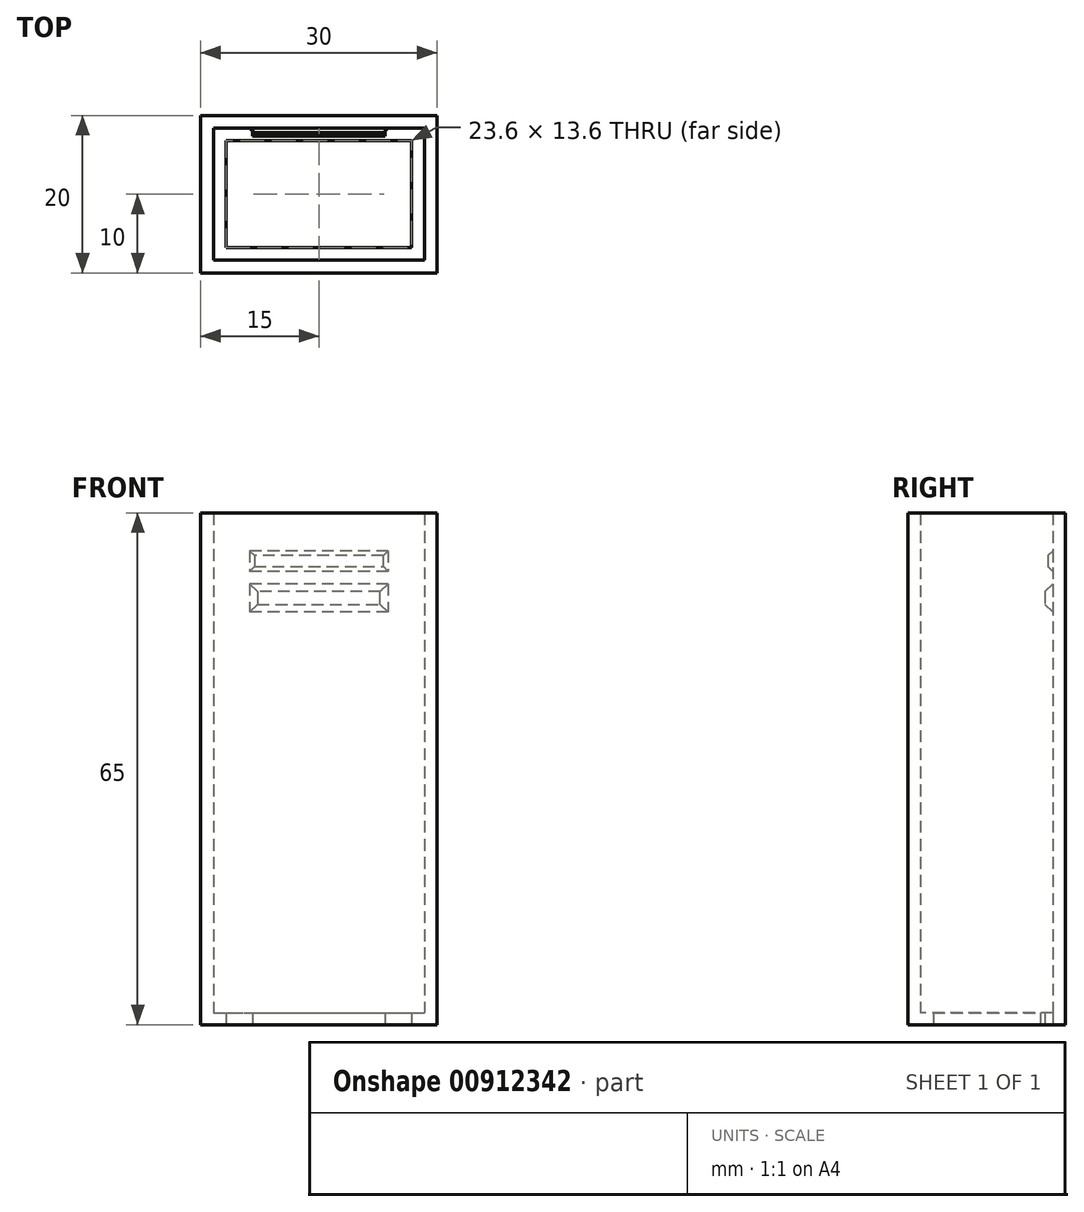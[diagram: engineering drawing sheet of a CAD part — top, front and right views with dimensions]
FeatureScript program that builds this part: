
annotation { "Feature Type Name" : "Feature", "Feature Type Description" : "" }
export const myFeature = defineFeature(function(context is Context, id is Id, definition is map)
    precondition{}
    {
        {
            var Q0;
            Q0=qCreatedBy(makeId("Top.planeOp"),FACE);
            var sketch = newSketch(context, id + "F0", { "sketchPlane" : qUnion([Q0])});
            skPoint(sketch, "E0.middle", {"position": v(0, 0) * mm});
            skLineSegment(sketch, "E1.bottom", {"start": v(-90, 80) * mm, "end": v(-60, 80) * mm});
            skLineSegment(sketch, "E1.top", {"start": v(-90, 60) * mm, "end": v(-60, 60) * mm});
            skLineSegment(sketch, "E1.left", {"start": v(-90, 80) * mm, "end": v(-90, 60) * mm});
            skLineSegment(sketch, "E1.right", {"start": v(-60, 80) * mm, "end": v(-60, 60) * mm});
            skLineSegment(sketch, "E2.bottom", {"start": v(-88.4, 78.4) * mm, "end": v(-61.6, 78.4) * mm});
            skLineSegment(sketch, "E2.top", {"start": v(-88.4, 61.6) * mm, "end": v(-61.6, 61.6) * mm});
            skLineSegment(sketch, "E2.left", {"start": v(-88.4, 78.4) * mm, "end": v(-88.4, 61.6) * mm});
            skLineSegment(sketch, "E2.right", {"start": v(-61.6, 78.4) * mm, "end": v(-61.6, 61.6) * mm});
            skLineSegment(sketch, "E3.bottom", {"start": v(-83.4, 78.4) * mm, "end": v(-66.6, 78.4) * mm});
            skLineSegment(sketch, "E3.top", {"start": v(-83.4, 77.4) * mm, "end": v(-66.6, 77.4) * mm});
            skLineSegment(sketch, "E3.left", {"start": v(-83.4, 78.4) * mm, "end": v(-83.4, 77.4) * mm});
            skLineSegment(sketch, "E3.right", {"start": v(-66.6, 78.4) * mm, "end": v(-66.6, 77.4) * mm});
            skLineSegment(sketch, "E4.bottom", {"start": v(-86.8, 63.2) * mm, "end": v(-63.2, 63.2) * mm});
            skLineSegment(sketch, "E4.top", {"start": v(-86.8, 76.8) * mm, "end": v(-63.2, 76.8) * mm});
            skLineSegment(sketch, "E4.left", {"start": v(-86.8, 63.2) * mm, "end": v(-86.8, 76.8) * mm});
            skLineSegment(sketch, "E4.right", {"start": v(-63.2, 63.2) * mm, "end": v(-63.2, 76.8) * mm});
            skSolve(sketch);
        }
        {
            var Q0;
            Q0=makeQuery(id+"F0.imprint","IMPRINT",FACE,{"disambiguationData":[TD([[makeQuery(id+"F0.imprint","IMPRINT",EDGE,{"derivedFrom":sQuery(id+"F0.wireOp",EDGE,"E1.bottom")}),-1.0]])]});
            extrude(context, id + "F1", {"entities" : qUnion([Q0]), "depth" : 65 * mm, "offsetDistance" : 25 * mm});
        }
        {
            var Q0;
            Q0=makeQuery(id+"F0.imprint","IMPRINT",FACE,{"disambiguationData":[TD([[makeQuery(id+"F0.imprint","IMPRINT",EDGE,{"derivedFrom":sQuery(id+"F0.wireOp",EDGE,"E2.top")}),1.0]])]});
            var Q1;
            Q1=makeQuery(id+"F0.imprint","IMPRINT",FACE,{"disambiguationData":[TD([[makeQuery(id+"F0.imprint","IMPRINT",EDGE,{"derivedFrom":sQuery(id+"F0.wireOp",EDGE,"E3.bottom")}),-1.0]])]});
            extrude(context, id + "F2", {"entities" : qUnion([Q0, Q1]), "operationType" : NewBodyOperationType.ADD, "depth" : 1.5 * mm, "offsetDistance" : 25 * mm});
        }
        {
            var Q0;
            Q0=makeQuery(id+"F1.opExtrude","SWEPT_FACE",FACE,{"disambiguationData":[OSD([sQuery(id+"F0.wireOp",EDGE,"E2.left")])]});
            var Q1;
            Q1=makeQuery(id+"F1.opExtrude","SWEPT_FACE",FACE,{"disambiguationData":[OSD([sQuery(id+"F0.wireOp",EDGE,"E2.right")])]});
            cPlane(context, id + "F3", {"entities" : qUnion([Q0, Q1]), "cplaneType" : CPlaneType.MID_PLANE, "offset" : 10 * mm, "oppositeDirection" : true, "width" : 150 * mm, "height" : 150 * mm});
        }
        {
            var Q0;
            Q0=qCreatedBy(id+"F3.planeOp",FACE);
            var sketch = newSketch(context, id + "F4", { "sketchPlane" : qUnion([Q0])});
            skLineSegment(sketch, "E5.bottom", {"start": v(78.4, 60.4) * mm, "end": v(77.8, 60.4) * mm});
            skLineSegment(sketch, "E5.top", {"start": v(78.4, 57.4) * mm, "end": v(77.8, 57.4) * mm});
            skLineSegment(sketch, "E5.left", {"start": v(78.4, 60.4) * mm, "end": v(78.4, 57.4) * mm});
            skLineSegment(sketch, "E5.right", {"start": v(77.8, 60.4) * mm, "end": v(77.8, 57.4) * mm});
            skLineSegment(sketch, "E6.bottom", {"start": v(78.4, 56.2) * mm, "end": v(77.4, 56.2) * mm});
            skLineSegment(sketch, "E6.top", {"start": v(78.4, 52.2) * mm, "end": v(77.4, 52.2) * mm});
            skLineSegment(sketch, "E6.left", {"start": v(78.4, 56.2) * mm, "end": v(78.4, 52.2) * mm});
            skLineSegment(sketch, "E6.right", {"start": v(77.4, 56.2) * mm, "end": v(77.4, 52.2) * mm});
            skSolve(sketch);
        }
        {
            var Q0;
            Q0 = qSketchRegion(id + "F4", true);
            extrude(context, id + "F5", {"entities" : qUnion([Q0]), "operationType" : NewBodyOperationType.ADD, "endBound" : BoundingType.SYMMETRIC, "depth" : 18 * mm, "offsetDistance" : 25 * mm});
        }
        {
            var Q0;
            Q0=makeQuery(id+"F5.opExtrude","SWEPT_EDGE",EDGE,{"disambiguationData":[OSD([sQuery(id+"F4.wireOp",EDGE,"E5.bottom"),sQuery(id+"F4.wireOp",EDGE,"E5.right")])]});
            var Q1;
            Q1=makeQuery(id+"F5.opExtrude","SWEPT_EDGE",EDGE,{"disambiguationData":[OSD([sQuery(id+"F4.wireOp",EDGE,"E5.top"),sQuery(id+"F4.wireOp",EDGE,"E5.right")])]});
            var Q2;
            Q2=makeQuery(id+"F5.opExtrude","CAP_EDGE",EDGE,{"disambiguationData":[OSD([sQuery(id+"F4.wireOp",EDGE,"E5.right")])],"isStart":true});
            var Q3;
            Q3=makeQuery(id+"F5.opExtrude","CAP_EDGE",EDGE,{"disambiguationData":[OSD([sQuery(id+"F4.wireOp",EDGE,"E5.right")])],"isStart":false});
            chamfer(context, id + "F6", {"entities" : qUnion([Q0, Q1, Q2, Q3]), "width" : 0.8 * mm, "tangentPropagation" : true});
        }
        {
            var Q0;
            Q0=makeQuery(id+"F5.opExtrude","SWEPT_EDGE",EDGE,{"disambiguationData":[OSD([sQuery(id+"F4.wireOp",EDGE,"E6.bottom"),sQuery(id+"F4.wireOp",EDGE,"E6.right")])]});
            var Q1;
            Q1=makeQuery(id+"F5.opExtrude","SWEPT_EDGE",EDGE,{"disambiguationData":[OSD([sQuery(id+"F4.wireOp",EDGE,"E6.top"),sQuery(id+"F4.wireOp",EDGE,"E6.right")])]});
            var Q2;
            Q2=makeQuery(id+"F5.opExtrude","CAP_EDGE",EDGE,{"disambiguationData":[OSD([sQuery(id+"F4.wireOp",EDGE,"E6.right")])],"isStart":true});
            var Q3;
            Q3=makeQuery(id+"F5.opExtrude","CAP_EDGE",EDGE,{"disambiguationData":[OSD([sQuery(id+"F4.wireOp",EDGE,"E6.right")])],"isStart":false});
            chamfer(context, id + "F7", {"entities" : qUnion([Q0, Q1, Q2, Q3]), "width" : 1.2 * mm, "tangentPropagation" : true});
        }
        {
            var Q0;
            Q0=makeQuery(id+"F1.opExtrude","CAP_FACE",FACE,{"disambiguationData":[OSD([sQuery(id+"F0.wireOp",EDGE,"E1.bottom"),sQuery(id+"F0.wireOp",EDGE,"E1.top"),sQuery(id+"F0.wireOp",EDGE,"E1.left"),sQuery(id+"F0.wireOp",EDGE,"E1.right"),sQuery(id+"F0.wireOp",EDGE,"E2.bottom"),sQuery(id+"F0.wireOp",EDGE,"E2.top"),sQuery(id+"F0.wireOp",EDGE,"E2.left"),sQuery(id+"F0.wireOp",EDGE,"E2.right"),sQuery(id+"F0.wireOp",EDGE,"E3.bottom")])],"isStart":false});
            var sketch = newSketch(context, id + "F8", { "sketchPlane" : qUnion([Q0])});
            skLineSegment(sketch, "E7", {"start": v(-88.4, 78.4) * mm, "end": v(-61.6, 61.6) * mm, "construction": true});
            skLineSegment(sketch, "E8", {"start": v(-61.6, 78.4) * mm, "end": v(-88.4, 61.6) * mm, "construction": true});
            skSolve(sketch);
        }
    });
